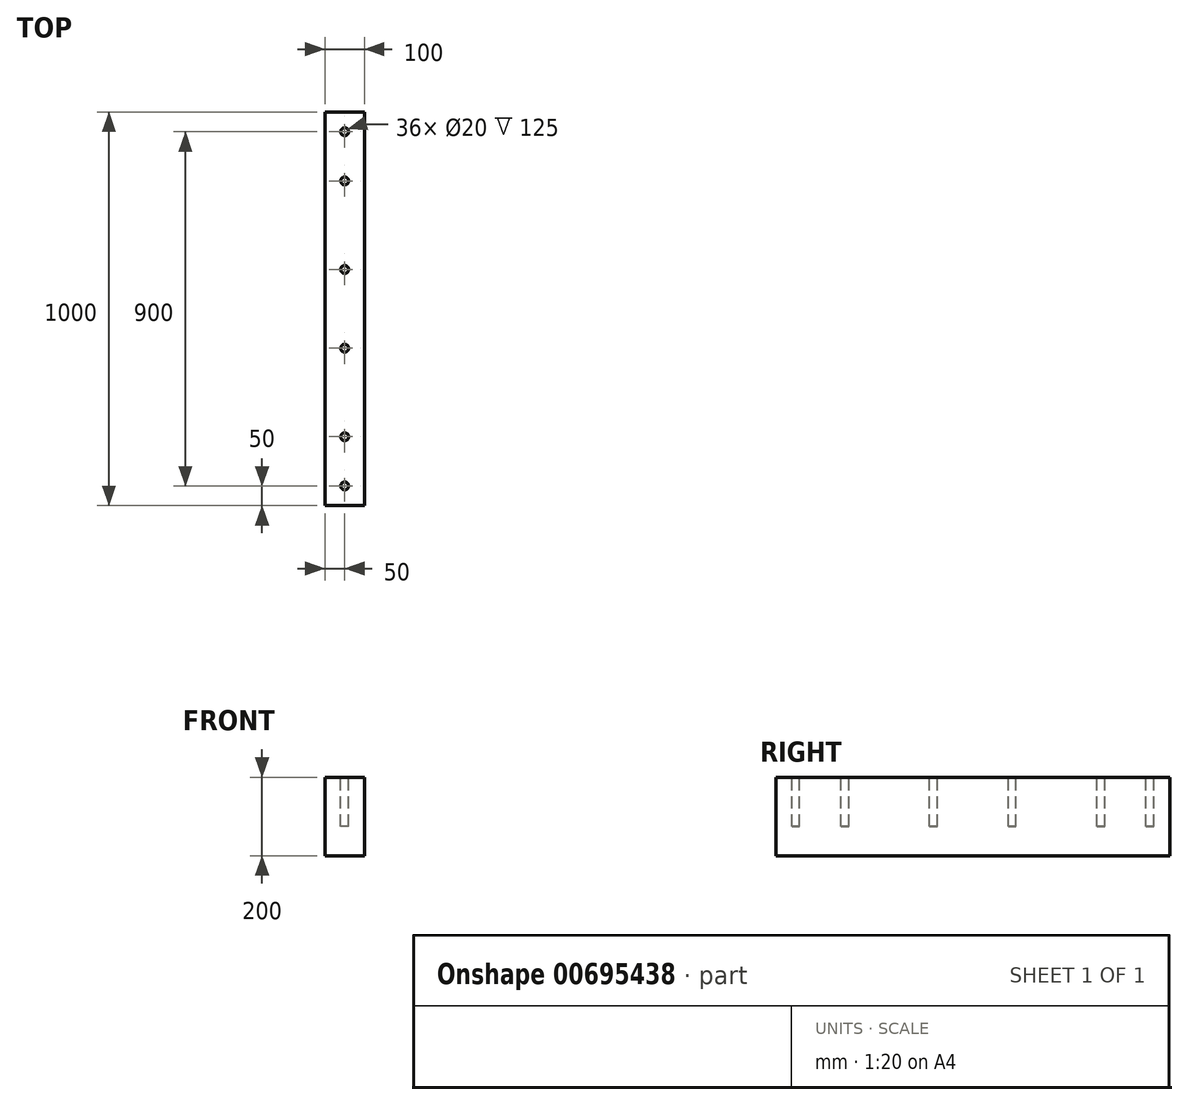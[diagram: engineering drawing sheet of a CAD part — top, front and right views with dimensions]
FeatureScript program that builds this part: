
annotation { "Feature Type Name" : "Feature", "Feature Type Description" : "" }
export const myFeature = defineFeature(function(context is Context, id is Id, definition is map)
    precondition{}
    {
        {
            var Q0;
            Q0=qCreatedBy(makeId("Front.planeOp"),FACE);
            var sketch = newSketch(context, id + "F0", { "sketchPlane" : qUnion([Q0])});
            skLineSegment(sketch, "E0.bottom", {"start": v(0, 0) * mm, "end": v(100, 0) * mm});
            skLineSegment(sketch, "E0.top", {"start": v(0, 200) * mm, "end": v(100, 200) * mm});
            skLineSegment(sketch, "E0.left", {"start": v(0, 0) * mm, "end": v(0, 200) * mm});
            skLineSegment(sketch, "E0.right", {"start": v(100, 0) * mm, "end": v(100, 200) * mm});
            skSolve(sketch);
        }
        {
            var Q0;
            Q0 = qSketchRegion(id + "F0", true);
            extrude(context, id + "F1", {"entities" : qUnion([Q0]), "depth" : 1000 * mm, "offsetDistance" : 25 * mm});
        }
        {
            var Q0;
            Q0=makeQuery(id+"F1.opExtrude","SWEPT_FACE",FACE,{"disambiguationData":[OSD([sQuery(id+"F0.wireOp",EDGE,"E0.top")])]});
            var sketch = newSketch(context, id + "F2", { "sketchPlane" : qUnion([Q0])});
            skCircle(sketch, "E1", {"center": v(50, -50) * mm, "radius": 10 * mm});
            skPoint(sketch, "E1.centerSnap0", {"position": v(50, 0) * mm});
            skCircle(sketch, "E2", {"center": v(50, -175) * mm, "radius": 10 * mm});
            skCircle(sketch, "E3", {"center": v(50, -400) * mm, "radius": 10 * mm});
            skCircle(sketch, "E4", {"center": v(50, -600) * mm, "radius": 10 * mm});
            skCircle(sketch, "E5", {"center": v(50, -950) * mm, "radius": 10 * mm});
            skPoint(sketch, "E5.centerSnap0", {"position": v(50, -1000) * mm});
            skCircle(sketch, "E6", {"center": v(50, -825) * mm, "radius": 10 * mm});
            skSolve(sketch);
        }
        {
            var Q0;
            Q0 = qSketchRegion(id + "F2", true);
            extrude(context, id + "F3", {"entities" : qUnion([Q0]), "operationType" : NewBodyOperationType.REMOVE, "oppositeDirection" : true, "depth" : 125 * mm, "offsetDistance" : 25 * mm});
        }
    });
